# Revit family: 210_3099b04aa1f543c2ab314b1538b732
name_source: partatom
category: Mechanical Equipment
revit_build: Autodesk Revit 2018 (Build: 20170223_1515(x64)
units: mm (PartAtom-declared; Revit-internal decimal feet)

## family parameters
Always vertical = Yes
Cut with Voids When Loaded = No
Part Type = Breaks Into
Room Calculation Point = No
Round Connector Dimension = Use Diameter
Shared = No
Work Plane-Based = No

## types (1)
- C2 R_R (700032)
    CAT0 = Yes
    Clearance Zone Front Depth = 650 mm  [stored 2.13255 ft]
    DEXH = 125 mm
    DEXT = 125 mm
    DEXT9 = 125 mm
    DL = 48 mm  [stored 0.15748 ft]
    DL__ve = -48 mm  [stored -0.15748 ft]
    DOUT = 125 mm
    DSUP = 125 mm
    Description = C2 R_R (700032)
    EXHY = 137 mm  [stored 0.449475 ft]
    EXT9X = 0 mm  [stored 0 ft]
    EXT9Y = 137 mm  [stored 0.449475 ft]
    EXTY = 137 mm  [stored 0.449475 ft]
    H = 523 mm  [stored 1.71588 ft]
    H2 = 262 mm  [stored 0.85958 ft]
    L2 = 450 mm  [stored 1.47638 ft]
    MC Product Code = C2 R_R (700032)
    Manufacturer = Flexit
    OUTY = 137 mm  [stored 0.449475 ft]
    QmdConnectorList = 221;DSUP;231;DOUT;241;DEXT;249;DEXT9;251;DEXH
    REXH = 63 mm
    REXT = 63 mm
    REXT9 = 63 mm
    ROUT = 63 mm
    RSUP = 63 mm
    SUPY = 137 mm  [stored 0.449475 ft]
    W = 351 mm  [stored 1.15157 ft]
    ZEXH = 141 mm
    ZEXT = 141 mm
    ZOUT = 381 mm  [stored 1.25 ft]
    ZSUP = 381 mm  [stored 1.25 ft]
    magiPartTypeId = 210
    magiProductFamilyId = 3099b04aa1f543c2ab314b1538b732
    magiProductId = 3099b04aa1f543c2ab314b1538b732

note: [stored X ft] marks values corroborated as IEEE doubles in the binary element streams (Revit-internal decimal feet)

## geometry (parser evidence)
native form markers: Sweep x1
no freeform markers — native parametric forms only
